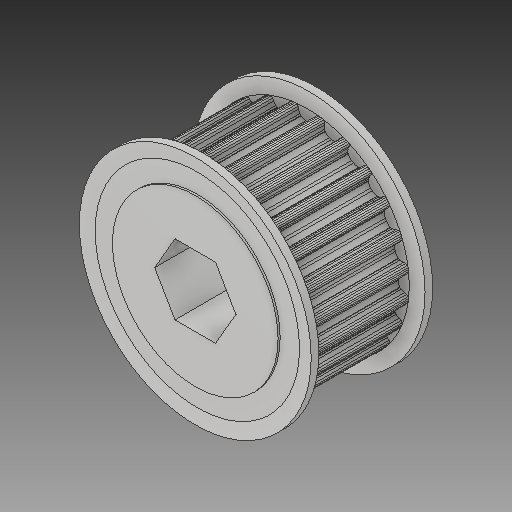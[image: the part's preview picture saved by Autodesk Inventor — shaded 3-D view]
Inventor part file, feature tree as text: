
AUTODESK INVENTOR PART (.ipt)
format: ipt  version: 2018 (Build 220112000, 112)  size: 710,656 bytes
history: native  units: in
note: dims shown in document units (in); Inventor stores cm internally (conversion verified against a paired STEP export)
features: mirror x1
ambient origin geometry x8: Origin, YZ Plane, XZ Plane, XY Plane, X Axis, Y Axis, Z Axis, Center Point
bodies: Solid1 (feature_tree)
feature tree (1):
  mirror  "Mirror1"
